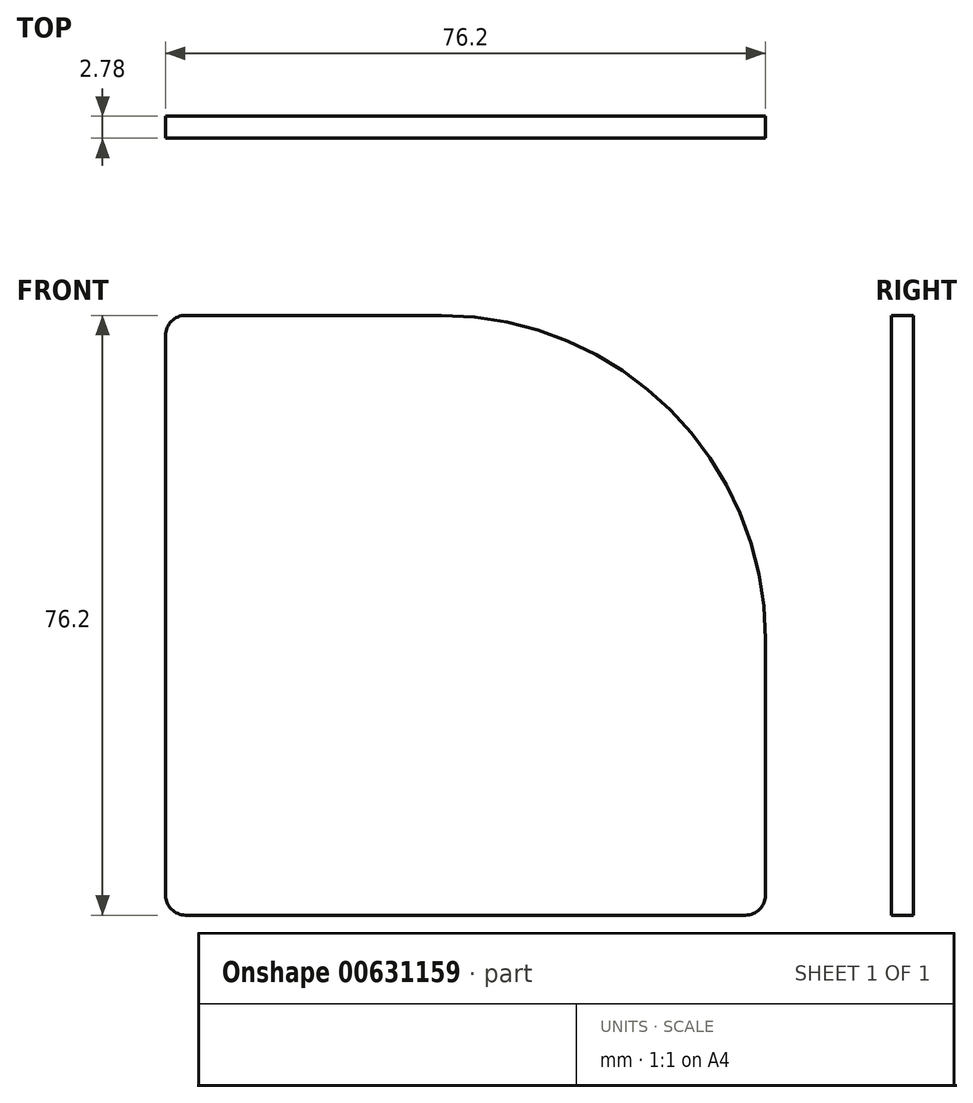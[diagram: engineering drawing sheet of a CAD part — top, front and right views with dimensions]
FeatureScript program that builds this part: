
annotation { "Feature Type Name" : "Feature", "Feature Type Description" : "" }
export const myFeature = defineFeature(function(context is Context, id is Id, definition is map)
    precondition{}
    {
        {
            var Q0;
            Q0=qCreatedBy(makeId("Front.planeOp"),FACE);
            var sketch = newSketch(context, id + "F0", { "sketchPlane" : qUnion([Q0])});
            skArc(sketch, "E0", {"start": v(41.15, 0) * mm, "mid": v(29.1, 29.1) * mm, "end": v(0, 41.15) * mm});
            skLineSegment(sketch, "E1", {"start": v(0, 0) * mm, "end": v(41.15, 0) * mm, "construction": true});
            skLineSegment(sketch, "E2", {"start": v(0, 0) * mm, "end": v(0, 41.15) * mm, "construction": true});
            skLineSegment(sketch, "E3", {"start": v(41.15, 0) * mm, "end": v(41.15, -35.05) * mm});
            skLineSegment(sketch, "E4", {"start": v(41.15, -35.05) * mm, "end": v(-35.05, -35.05) * mm});
            skLineSegment(sketch, "E5", {"start": v(-35.05, -35.05) * mm, "end": v(-35.05, 41.15) * mm});
            skLineSegment(sketch, "E6", {"start": v(-35.05, 41.15) * mm, "end": v(0, 41.15) * mm});
            skSolve(sketch);
        }
        {
            var Q0;
            Q0 = qSketchRegion(id + "F0", true);
            var Q1;
            Q1=sQuery(id+"F0.wireOp",EDGE,"E2");
            var Q2;
            Q2=sQuery(id+"F0.wireOp",EDGE,"E1");
            extrude(context, id + "F1", {"entities" : qUnion([Q0]), "surfaceEntities" : qUnion([Q1, Q2]), "depth" : 2.78 * mm, "offsetDistance" : 25.4 * mm});
        }
        {
            var Q0;
            Q0=makeQuery(id+"F1.opExtrude","SWEPT_EDGE",EDGE,{"disambiguationData":[OSD([sQuery(id+"F0.wireOp",EDGE,"E4"),sQuery(id+"F0.wireOp",EDGE,"E5")])]});
            var Q1;
            Q1=makeQuery(id+"F1.opExtrude","SWEPT_EDGE",EDGE,{"disambiguationData":[OSD([sQuery(id+"F0.wireOp",EDGE,"E5"),sQuery(id+"F0.wireOp",EDGE,"E6")])]});
            var Q2;
            Q2=makeQuery(id+"F1.opExtrude","SWEPT_EDGE",EDGE,{"disambiguationData":[OSD([sQuery(id+"F0.wireOp",EDGE,"E3"),sQuery(id+"F0.wireOp",EDGE,"E4")])]});
            fillet(context, id + "F2", {"entities" : qUnion([Q0, Q1, Q2]), "radius" : 2.54 * mm, "tangentPropagation" : true, "allowEdgeOverflow" : false});
        }
    });
